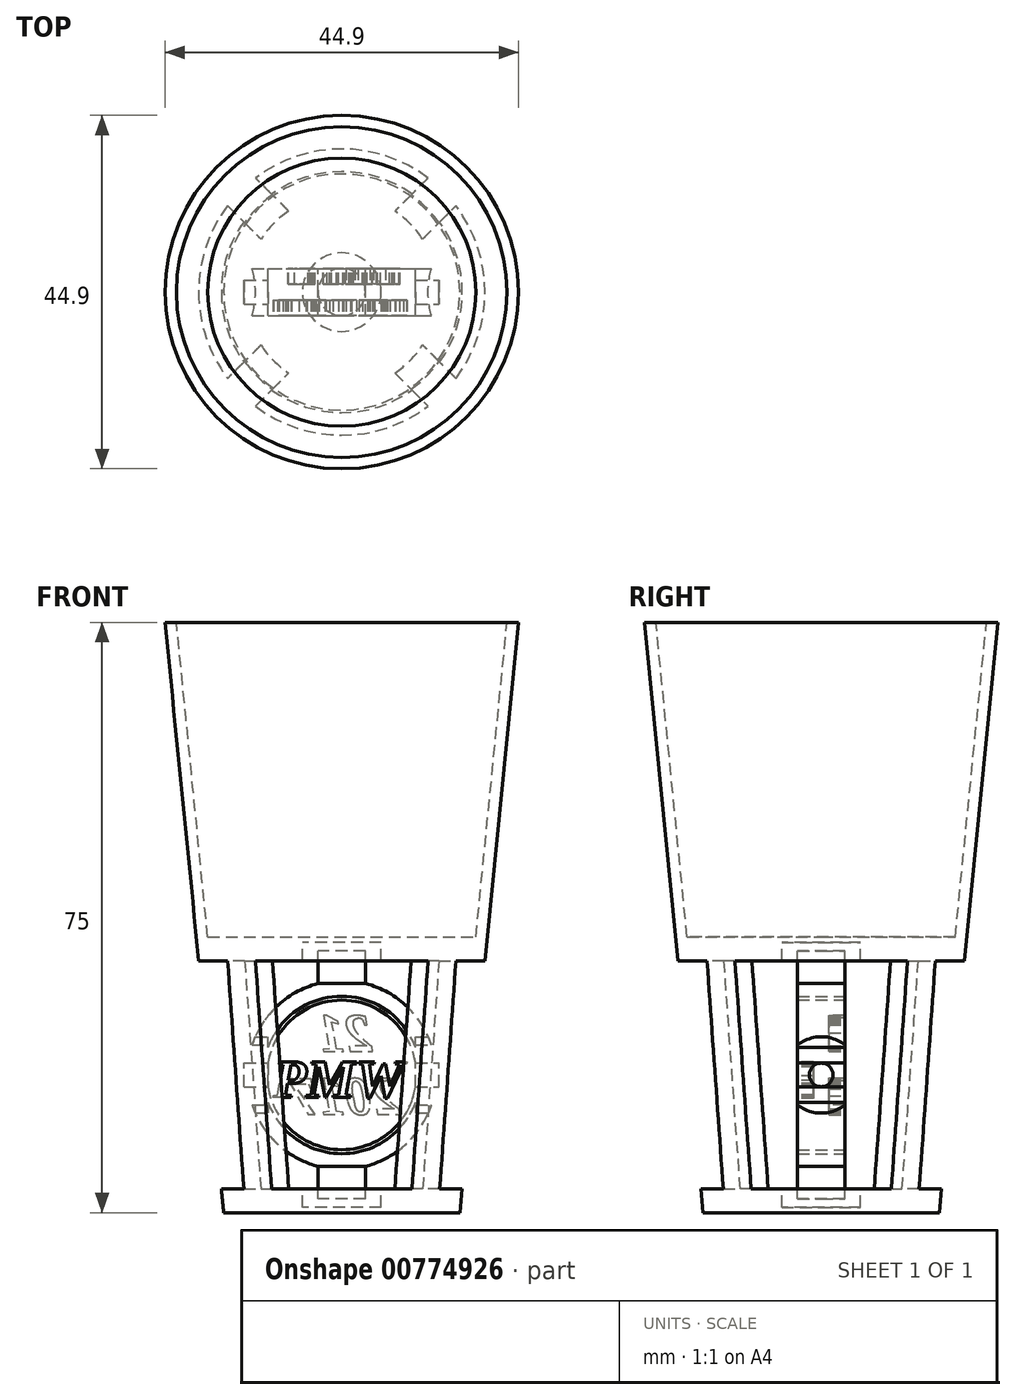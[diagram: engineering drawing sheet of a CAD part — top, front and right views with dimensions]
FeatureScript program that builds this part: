
annotation { "Feature Type Name" : "Feature", "Feature Type Description" : "" }
export const myFeature = defineFeature(function(context is Context, id is Id, definition is map)
    precondition{}
    {
        {
            var Q0;
            Q0=qCreatedBy(makeId("Front.planeOp"),FACE);
            var sketch = newSketch(context, id + "F0", { "sketchPlane" : qUnion([Q0])});
            skLineSegment(sketch, "E0", {"start": v(0, 0) * mm, "end": v(15, 0) * mm});
            skLineSegment(sketch, "E1", {"start": v(15, 0) * mm, "end": v(22.45, 75) * mm});
            skLineSegment(sketch, "E2", {"start": v(22.45, 75) * mm, "end": v(21, 75) * mm});
            skLineSegment(sketch, "E3", {"start": v(21, 75) * mm, "end": v(17.03, 35) * mm});
            skLineSegment(sketch, "E4", {"start": v(17.03, 35) * mm, "end": v(0, 35) * mm});
            skLineSegment(sketch, "E5", {"start": v(12.28, 3) * mm, "end": v(15.16, 32) * mm});
            skLineSegment(sketch, "E6", {"start": v(15.16, 32) * mm, "end": v(0, 32) * mm});
            skLineSegment(sketch, "E7", {"start": v(12.28, 3) * mm, "end": v(0, 3) * mm});
            skLineSegment(sketch, "E8.trimOffspring", {"start": v(0, 3) * mm, "end": v(0, 0) * mm});
            skLineSegment(sketch, "E9", {"start": v(0, 32) * mm, "end": v(0, 35) * mm});
            skSolve(sketch);
        }
        {
            var Q0;
            Q0=qSketchRegion(id+"F0",true);
            var Q1;
            Q1=sQuery(id+"F0.wireOp",EDGE,"E9");
            revolve(context, id + "F1", {"surfaceOperationType" : NewSurfaceOperationType.NEW, "entities" : qUnion([Q0]), "axis" : qUnion([Q1]), "revolveType" : RevolveType.FULL});
        }
        {
            var Q0;
            Q0=makeQuery(id+"F1.opRevolve","SWEPT_FACE",FACE,{"disambiguationData":[OSD([sQuery(id+"F0.wireOp",EDGE,"E7")])]});
            var sketch = newSketch(context, id + "F2", { "sketchPlane" : qUnion([Q0])});
            skArc(sketch, "E10", {"start": v(15.68, 19.22) * mm, "mid": v(0, 24.8) * mm, "end": v(-15.68, 19.22) * mm});
            skLineSegment(sketch, "E11", {"start": v(0, 0) * mm, "end": v(0, 28.4) * mm, "construction": true});
            skLineSegment(sketch, "E12", {"start": v(0, 0) * mm, "end": v(28.58, 0) * mm, "construction": true});
            skLineSegment(sketch, "E13", {"start": v(0, 0) * mm, "end": v(20.34, 20.34) * mm, "construction": true});
            skLineSegment(sketch, "E14", {"start": v(15.8, 12.26) * mm, "end": v(19.22, 15.68) * mm});
            skLineSegment(sketch, "E15.MirrorCS", {"start": v(12.26, 15.8) * mm, "end": v(15.68, 19.22) * mm});
            skLineSegment(sketch, "E16.MirrorCS", {"start": v(-15.8, 12.26) * mm, "end": v(-19.22, 15.68) * mm});
            skLineSegment(sketch, "E17.MirrorCS", {"start": v(-12.26, 15.8) * mm, "end": v(-15.68, 19.22) * mm});
            skLineSegment(sketch, "E18.MirrorCS", {"start": v(12.26, -15.8) * mm, "end": v(15.68, -19.22) * mm});
            skLineSegment(sketch, "E19.MirrorCS", {"start": v(-12.26, -15.8) * mm, "end": v(-15.68, -19.22) * mm});
            skLineSegment(sketch, "E20.MirrorCS", {"start": v(15.8, -12.26) * mm, "end": v(19.22, -15.68) * mm});
            skLineSegment(sketch, "E21.MirrorCS", {"start": v(-15.8, -12.26) * mm, "end": v(-19.22, -15.68) * mm});
            skPoint(sketch, "E22.end.orphan", {"position": v(19.93, 19.93) * mm});
            skPoint(sketch, "E22.start.orphan", {"position": v(21.7, 18.16) * mm});
            skPoint(sketch, "E23.MirrorCS.start.orphan", {"position": v(18.16, 21.7) * mm});
            skPoint(sketch, "E24.orphan", {"position": v(-18.16, 21.7) * mm});
            skPoint(sketch, "E25.MirrorCS.end.orphan", {"position": v(-19.93, 19.93) * mm});
            skPoint(sketch, "E26.MirrorCS.start.orphan", {"position": v(-21.7, 18.16) * mm});
            skArc(sketch, "E27.trimOffspring", {"start": v(-19.22, 15.68) * mm, "mid": v(-24.8, 0) * mm, "end": v(-19.22, -15.68) * mm});
            skPoint(sketch, "E28.orphan", {"position": v(-18.16, -21.7) * mm});
            skPoint(sketch, "E29.MirrorCS.end.orphan", {"position": v(-19.93, -19.93) * mm});
            skPoint(sketch, "E30.MirrorCS.start.orphan", {"position": v(-21.7, -18.16) * mm});
            skArc(sketch, "E31.trimOffspring", {"start": v(-15.68, -19.22) * mm, "mid": v(0, -24.8) * mm, "end": v(15.68, -19.22) * mm});
            skPoint(sketch, "E32.MirrorCS.end.orphan", {"position": v(19.93, -19.93) * mm});
            skPoint(sketch, "E32.MirrorCS.start.orphan", {"position": v(21.7, -18.16) * mm});
            skPoint(sketch, "E33.MirrorCS.start.orphan", {"position": v(18.16, -21.7) * mm});
            skArc(sketch, "E34.trimOffspring", {"start": v(19.22, -15.68) * mm, "mid": v(24.8, 0) * mm, "end": v(19.22, 15.68) * mm});
            skArc(sketch, "E35", {"start": v(-8.61, 5.08) * mm, "mid": v(-10, 0) * mm, "end": v(-8.61, -5.08) * mm});
            skLineSegment(sketch, "E36", {"start": v(-12.26, -15.8) * mm, "end": v(-5.08, -8.61) * mm});
            skLineSegment(sketch, "E37", {"start": v(-15.8, -12.26) * mm, "end": v(-8.61, -5.08) * mm});
            skLineSegment(sketch, "E38", {"start": v(12.26, -15.8) * mm, "end": v(5.08, -8.61) * mm});
            skLineSegment(sketch, "E39", {"start": v(15.8, -12.26) * mm, "end": v(8.61, -5.08) * mm});
            skLineSegment(sketch, "E40", {"start": v(15.8, 12.26) * mm, "end": v(8.61, 5.08) * mm});
            skLineSegment(sketch, "E41", {"start": v(12.26, 15.8) * mm, "end": v(5.08, 8.61) * mm});
            skLineSegment(sketch, "E42", {"start": v(-12.26, 15.8) * mm, "end": v(-5.08, 8.61) * mm});
            skLineSegment(sketch, "E43", {"start": v(-15.8, 12.26) * mm, "end": v(-8.61, 5.08) * mm});
            skArc(sketch, "E44.trimOffspring", {"start": v(5.08, 8.61) * mm, "mid": v(0, 10) * mm, "end": v(-5.08, 8.61) * mm});
            skArc(sketch, "E45.trimOffspring", {"start": v(8.61, -5.08) * mm, "mid": v(10, 0) * mm, "end": v(8.61, 5.08) * mm});
            skArc(sketch, "E46.trimOffspring", {"start": v(-5.08, -8.61) * mm, "mid": v(0, -10) * mm, "end": v(5.08, -8.61) * mm});
            skSolve(sketch);
        }
        {
            var Q0;
            Q0=qSketchRegion(id+"F2",true);
            extrude(context, id + "F3", {"entities" : qUnion([Q0]), "operationType" : NewBodyOperationType.REMOVE, "depth" : 29 * mm, "offsetDistance" : 25 * mm});
        }
        {
            var Q0;
            Q0=makeQuery(id+"F3.boolean.opBoolean","MERGE",FACE,{"derivedFrom":[makeQuery(id+"F1.opRevolve","SWEPT_FACE",FACE,{"disambiguationData":[OSD([sQuery(id+"F0.wireOp",EDGE,"E7")])]}),makeQuery(id+"F3.opExtrude","CAP_FACE",FACE,{"disambiguationData":[OSD([sQuery(id+"F2.wireOp",EDGE,"E10"),sQuery(id+"F2.wireOp",EDGE,"E15.MirrorCS"),sQuery(id+"F2.wireOp",EDGE,"E17.MirrorCS"),sQuery(id+"F2.wireOp",EDGE,"E41"),sQuery(id+"F2.wireOp",EDGE,"E42"),sQuery(id+"F2.wireOp",EDGE,"E44.trimOffspring")])],"isStart":true}),makeQuery(id+"F3.opExtrude","CAP_FACE",FACE,{"disambiguationData":[OSD([sQuery(id+"F2.wireOp",EDGE,"E14"),sQuery(id+"F2.wireOp",EDGE,"E20.MirrorCS"),sQuery(id+"F2.wireOp",EDGE,"E34.trimOffspring"),sQuery(id+"F2.wireOp",EDGE,"E39"),sQuery(id+"F2.wireOp",EDGE,"E40"),sQuery(id+"F2.wireOp",EDGE,"E45.trimOffspring")])],"isStart":true}),makeQuery(id+"F3.opExtrude","CAP_FACE",FACE,{"disambiguationData":[OSD([sQuery(id+"F2.wireOp",EDGE,"E16.MirrorCS"),sQuery(id+"F2.wireOp",EDGE,"E21.MirrorCS"),sQuery(id+"F2.wireOp",EDGE,"E27.trimOffspring"),sQuery(id+"F2.wireOp",EDGE,"E35"),sQuery(id+"F2.wireOp",EDGE,"E37"),sQuery(id+"F2.wireOp",EDGE,"E43")])],"isStart":true}),makeQuery(id+"F3.opExtrude","CAP_FACE",FACE,{"disambiguationData":[OSD([sQuery(id+"F2.wireOp",EDGE,"E18.MirrorCS"),sQuery(id+"F2.wireOp",EDGE,"E19.MirrorCS"),sQuery(id+"F2.wireOp",EDGE,"E31.trimOffspring"),sQuery(id+"F2.wireOp",EDGE,"E36"),sQuery(id+"F2.wireOp",EDGE,"E38"),sQuery(id+"F2.wireOp",EDGE,"E46.trimOffspring")])],"isStart":true})]});
            var sketch = newSketch(context, id + "F4", { "sketchPlane" : qUnion([Q0])});
            skCircle(sketch, "E47", {"center": v(0, 0) * mm, "radius": 3.5 * mm});
            skSolve(sketch);
        }
        {
            var Q0;
            Q0=qSketchRegion(id+"F4",true);
            extrude(context, id + "F5", {"entities" : qUnion([Q0]), "operationType" : NewBodyOperationType.REMOVE, "oppositeDirection" : true, "depth" : 2 * mm, "offsetDistance" : 25 * mm, "hasSecondDirection" : true, "secondDirectionOppositeDirection" : false, "secondDirectionDepth" : 31 * mm});
        }
        {
            var Q0;
            Q0=qCreatedBy(makeId("Front.planeOp"),FACE);
            var sketch = newSketch(context, id + "F6", { "sketchPlane" : qUnion([Q0])});
            skLineSegment(sketch, "E48", {"start": v(0, 33.25) * mm, "end": v(3, 33.25) * mm});
            skLineSegment(sketch, "E49", {"start": v(3, 33.25) * mm, "end": v(3, 29.12) * mm});
            skLineSegment(sketch, "E50", {"start": v(3, 29.12) * mm, "end": v(3, 29.12) * mm});
            skArc(sketch, "E51", {"start": v(3, 5.88) * mm, "mid": v(12, 17.5) * mm, "end": v(3, 29.12) * mm});
            skLineSegment(sketch, "E52", {"start": v(3, 5.88) * mm, "end": v(3, 1.75) * mm});
            skLineSegment(sketch, "E53", {"start": v(3, 1.75) * mm, "end": v(0, 1.75) * mm});
            skLineSegment(sketch, "E54.MirrorCS", {"start": v(0, 33.25) * mm, "end": v(-3, 33.25) * mm});
            skLineSegment(sketch, "E55.MirrorCS", {"start": v(-3, 33.25) * mm, "end": v(-3, 29.12) * mm});
            skLineSegment(sketch, "E56.MirrorCS", {"start": v(-3, 1.75) * mm, "end": v(0, 1.75) * mm});
            skLineSegment(sketch, "E57.MirrorCS", {"start": v(-3, 5.88) * mm, "end": v(-3, 1.75) * mm});
            skArc(sketch, "E58.MirrorCS", {"start": v(-3, 5.88) * mm, "mid": v(-12, 17.5) * mm, "end": v(-3, 29.12) * mm});
            skCircle(sketch, "E59", {"center": v(0, 17.5) * mm, "radius": 10 * mm});
            skSolve(sketch);
        }
        {
            var Q0;
            Q0=qSketchRegion(id+"F6",true);
            extrude(context, id + "F7", {"entities" : qUnion([Q0]), "endBound" : BoundingType.SYMMETRIC, "depth" : 6 * mm, "offsetDistance" : 25 * mm});
        }
        {
            var Q0;
            Q0=qCreatedBy(makeId("Right.planeOp"),FACE);
            var sketch = newSketch(context, id + "F8", { "sketchPlane" : qUnion([Q0])});
            skCircle(sketch, "E60", {"center": v(0, 17.5) * mm, "radius": 2 * mm});
            skSolve(sketch);
        }
        {
            var Q0;
            Q0=qSketchRegion(id+"F8",true);
            extrude(context, id + "F9", {"entities" : qUnion([Q0]), "operationType" : NewBodyOperationType.REMOVE, "endBound" : BoundingType.SYMMETRIC, "depth" : 30 * mm, "offsetDistance" : 25 * mm});
        }
        {
            var Q0;
            Q0=qCreatedBy(makeId("Front.planeOp"),FACE);
            var sketch = newSketch(context, id + "F10", { "sketchPlane" : qUnion([Q0])});
            skArc(sketch, "E61", {"start": v(9.38, 19) * mm, "mid": v(0, 27) * mm, "end": v(-9.38, 19) * mm});
            skLineSegment(sketch, "E62", {"start": v(-13.8, 17.5) * mm, "end": v(14.42, 17.5) * mm, "construction": true});
            skLineSegment(sketch, "E63", {"start": v(9.38, 16) * mm, "end": v(12.38, 16) * mm});
            skLineSegment(sketch, "E64", {"start": v(12.38, 16) * mm, "end": v(12.38, 17.5) * mm});
            skLineSegment(sketch, "E65.MirrorCS", {"start": v(9.38, 19) * mm, "end": v(12.38, 19) * mm});
            skLineSegment(sketch, "E66.MirrorCS", {"start": v(12.38, 19) * mm, "end": v(12.38, 17.5) * mm});
            skLineSegment(sketch, "E67.MirrorCS", {"start": v(-9.38, 16) * mm, "end": v(-12.38, 16) * mm});
            skLineSegment(sketch, "E68.MirrorCS", {"start": v(-12.38, 19) * mm, "end": v(-12.38, 17.5) * mm});
            skLineSegment(sketch, "E69.MirrorCS", {"start": v(-12.38, 16) * mm, "end": v(-12.38, 17.5) * mm});
            skLineSegment(sketch, "E70.MirrorCS", {"start": v(-9.38, 19) * mm, "end": v(-12.38, 19) * mm});
            skArc(sketch, "E71.trimOffspring", {"start": v(-9.38, 16) * mm, "mid": v(0, 8) * mm, "end": v(9.38, 16) * mm});
            skSolve(sketch);
        }
        {
            var Q0;
            Q0=qSketchRegion(id+"F10",true);
            extrude(context, id + "F11", {"entities" : qUnion([Q0]), "endBound" : BoundingType.SYMMETRIC, "depth" : 6 * mm, "offsetDistance" : 25 * mm});
        }
        {
            var Q0;
            Q0=qCreatedBy(makeId("Front.planeOp"),FACE);
            var sketch = newSketch(context, id + "F12", { "sketchPlane" : qUnion([Q0])});
            skLineSegment(sketch, "E72.0", {"start": v(3, 33.25) * mm, "end": v(3, 29.12) * mm});
            skLineSegment(sketch, "E73.0", {"start": v(0, 33.25) * mm, "end": v(3, 33.25) * mm});
            skLineSegment(sketch, "E74", {"start": v(0, 33.25) * mm, "end": v(0, 34.3) * mm});
            skLineSegment(sketch, "E75", {"start": v(0, 34.3) * mm, "end": v(5, 34.3) * mm});
            skLineSegment(sketch, "E76", {"start": v(5, 34.3) * mm, "end": v(5, 29.12) * mm});
            skLineSegment(sketch, "E77", {"start": v(5, 29.12) * mm, "end": v(3, 29.12) * mm});
            skLineSegment(sketch, "E78", {"start": v(0, 17.5) * mm, "end": v(16.9, 17.5) * mm, "construction": true});
            skLineSegment(sketch, "E79.MirrorCS", {"start": v(5, 5.88) * mm, "end": v(3, 5.88) * mm});
            skLineSegment(sketch, "E80.MirrorCS", {"start": v(5, 0.7) * mm, "end": v(5, 5.88) * mm});
            skLineSegment(sketch, "E81.MirrorCS", {"start": v(0, 0.7) * mm, "end": v(5, 0.7) * mm});
            skLineSegment(sketch, "E82.MirrorCS", {"start": v(3, 1.75) * mm, "end": v(3, 5.88) * mm});
            skLineSegment(sketch, "E83.MirrorCS", {"start": v(0, 1.75) * mm, "end": v(3, 1.75) * mm});
            skLineSegment(sketch, "E84.MirrorCS", {"start": v(0, 1.75) * mm, "end": v(0, 0.7) * mm});
            skSolve(sketch);
        }
        {
            var Q0;
            Q0=qSketchRegion(id+"F12",true);
            var Q1;
            Q1=sQuery(id+"F12.wireOp",EDGE,"E74");
            revolve(context, id + "F13", {"operationType" : NewBodyOperationType.REMOVE, "surfaceOperationType" : NewSurfaceOperationType.NEW, "entities" : qUnion([Q0]), "axis" : qUnion([Q1]), "revolveType" : RevolveType.FULL, "oppositeDirection" : true});
        }
        {
            var Q0;
            Q0=qCreatedBy(makeId("Front.planeOp"),FACE);
            var sketch = newSketch(context, id + "F14", { "sketchPlane" : qUnion([Q0])});
            skLineSegment(sketch, "E85.0", {"start": v(9.38, 19) * mm, "end": v(12.38, 19) * mm});
            skLineSegment(sketch, "E86.0", {"start": v(12.38, 17.5) * mm, "end": v(12.38, 19) * mm});
            skLineSegment(sketch, "E87", {"start": v(0, 17.5) * mm, "end": v(17.25, 17.5) * mm, "construction": true});
            skPoint(sketch, "E88.orphan", {"position": v(12.38, 16) * mm});
            skLineSegment(sketch, "E89", {"start": v(9.38, 19) * mm, "end": v(9.38, 22.35) * mm});
            skLineSegment(sketch, "E90", {"start": v(9.38, 22.35) * mm, "end": v(15, 22.35) * mm});
            skLineSegment(sketch, "E91", {"start": v(15, 22.35) * mm, "end": v(15, 17.5) * mm});
            skLineSegment(sketch, "E92", {"start": v(15, 17.5) * mm, "end": v(12.38, 17.5) * mm});
            skLineSegment(sketch, "E93.MirrorCS", {"start": v(-12.38, 17.5) * mm, "end": v(-12.38, 19) * mm});
            skLineSegment(sketch, "E94.MirrorCS", {"start": v(-9.38, 22.35) * mm, "end": v(-15, 22.35) * mm});
            skLineSegment(sketch, "E95.MirrorCS", {"start": v(-9.38, 19) * mm, "end": v(-9.38, 22.35) * mm});
            skLineSegment(sketch, "E96.MirrorCS", {"start": v(-15, 22.35) * mm, "end": v(-15, 17.5) * mm});
            skLineSegment(sketch, "E97.MirrorCS", {"start": v(-15, 17.5) * mm, "end": v(-12.38, 17.5) * mm});
            skLineSegment(sketch, "E98.MirrorCS", {"start": v(-9.38, 19) * mm, "end": v(-12.38, 19) * mm});
            skSolve(sketch);
        }
        {
            var Q0;
            Q0=qSketchRegion(id+"F14",true);
            var Q1;
            Q1=sQuery(id+"F14.wireOp",EDGE,"E97.MirrorCS");
            revolve(context, id + "F15", {"operationType" : NewBodyOperationType.REMOVE, "surfaceOperationType" : NewSurfaceOperationType.NEW, "entities" : qUnion([Q0]), "axis" : qUnion([Q1]), "revolveType" : RevolveType.FULL, "oppositeDirection" : true});
        }
        {
            var Q0;
            Q0=makeQuery(id+"F11.opExtrude","CAP_FACE",FACE,{"disambiguationData":[OSD([sQuery(id+"F10.wireOp",EDGE,"E61"),sQuery(id+"F10.wireOp",EDGE,"E63"),sQuery(id+"F10.wireOp",EDGE,"E64"),sQuery(id+"F10.wireOp",EDGE,"E65.MirrorCS"),sQuery(id+"F10.wireOp",EDGE,"E66.MirrorCS"),sQuery(id+"F10.wireOp",EDGE,"E67.MirrorCS"),sQuery(id+"F10.wireOp",EDGE,"E68.MirrorCS"),sQuery(id+"F10.wireOp",EDGE,"E69.MirrorCS"),sQuery(id+"F10.wireOp",EDGE,"E70.MirrorCS"),sQuery(id+"F10.wireOp",EDGE,"E71.trimOffspring")])],"isStart":false});
            var sketch = newSketch(context, id + "F16", { "sketchPlane" : qUnion([Q0])});
            skText(sketch, "E99", { "text": "PMW", "fontName": "Tinos-BoldItalic.ttf"});
            const initialGuessF16  = {"E99": [-0.00872, 0.01462, 1, 0, 0.005]};
            skSetInitialGuess(sketch, initialGuessF16);
            skSolve(sketch);
        }
        {
            var Q0;
            Q0=qSketchRegion(id+"F16",true);
            extrude(context, id + "F17", {"entities" : qUnion([Q0]), "operationType" : NewBodyOperationType.REMOVE, "oppositeDirection" : true, "depth" : 2 * mm, "offsetDistance" : 25 * mm});
        }
        {
            var Q0;
            Q0=makeQuery(id+"F11.opExtrude","CAP_FACE",FACE,{"disambiguationData":[OSD([sQuery(id+"F10.wireOp",EDGE,"E61"),sQuery(id+"F10.wireOp",EDGE,"E63"),sQuery(id+"F10.wireOp",EDGE,"E64"),sQuery(id+"F10.wireOp",EDGE,"E65.MirrorCS"),sQuery(id+"F10.wireOp",EDGE,"E66.MirrorCS"),sQuery(id+"F10.wireOp",EDGE,"E67.MirrorCS"),sQuery(id+"F10.wireOp",EDGE,"E68.MirrorCS"),sQuery(id+"F10.wireOp",EDGE,"E69.MirrorCS"),sQuery(id+"F10.wireOp",EDGE,"E70.MirrorCS"),sQuery(id+"F10.wireOp",EDGE,"E71.trimOffspring")])],"isStart":true});
            var sketch = newSketch(context, id + "F18", { "sketchPlane" : qUnion([Q0])});
            skText(sketch, "E100", { "text": "  21\n2017", "fontName": "Tinos-BoldItalic.ttf"});
            const initialGuessF18  = {"E100": [-0.00732, 0.02046, 1, 0, 0.005]};
            skSetInitialGuess(sketch, initialGuessF18);
            skSolve(sketch);
        }
        {
            var Q0;
            Q0=qSketchRegion(id+"F18",true);
            extrude(context, id + "F19", {"entities" : qUnion([Q0]), "operationType" : NewBodyOperationType.REMOVE, "oppositeDirection" : true, "depth" : 2 * mm, "offsetDistance" : 25 * mm});
        }
        {
            var Q0;
            Q0=qCreatedBy(makeId("Front.planeOp"),FACE);
            var sketch = newSketch(context, id + "F20", { "sketchPlane" : qUnion([Q0])});
            skLineSegment(sketch, "E101", {"start": v(21, 74.98) * mm, "end": v(17.03, 34.98) * mm});
            skLineSegment(sketch, "E102", {"start": v(-17.03, 34.98) * mm, "end": v(-20.5, 69.95) * mm});
            skLineSegment(sketch, "E103", {"start": v(20.5, 69.95) * mm, "end": v(17.03, 34.98) * mm});
            skLineSegment(sketch, "E104", {"start": v(21, 74.98) * mm, "end": v(0, 74.98) * mm});
            skLineSegment(sketch, "E105", {"start": v(0, 74.98) * mm, "end": v(0, 34.98) * mm});
            skLineSegment(sketch, "E106", {"start": v(0, 34.98) * mm, "end": v(17.03, 34.98) * mm});
            skSolve(sketch);
        }
        {
            var Q0;
            {var subQ0=sQuery(id+"F20.wireOp",EDGE,"E104");Q0=makeQuery(id+"F20.imprint","IMPRINT",FACE,{"disambiguationData":[TD([[makeQuery(id+"F20.imprint","IMPRINT",EDGE,{"derivedFrom":subQ0}),1.0]])]});}
            var Q1;
            Q1=sQuery(id+"F20.wireOp",EDGE,"E105");
            revolve(context, id + "F21", {"surfaceOperationType" : NewSurfaceOperationType.NEW, "entities" : qUnion([Q0]), "axis" : qUnion([Q1]), "revolveType" : RevolveType.FULL});
        }
        {
            var Q0;
            Q0=makeQuery(id+"F21.opRevolve","SWEPT_BODY",BODY,{"disambiguationData":[OSD([sQuery(id+"F20.wireOp",EDGE,"E101"),sQuery(id+"F20.wireOp",EDGE,"E104"),sQuery(id+"F20.wireOp",EDGE,"E105"),sQuery(id+"F20.wireOp",EDGE,"E106")])]});
            deleteBodies(context, id + "F22", {"entities" : qUnion([Q0])});
        }
    });
